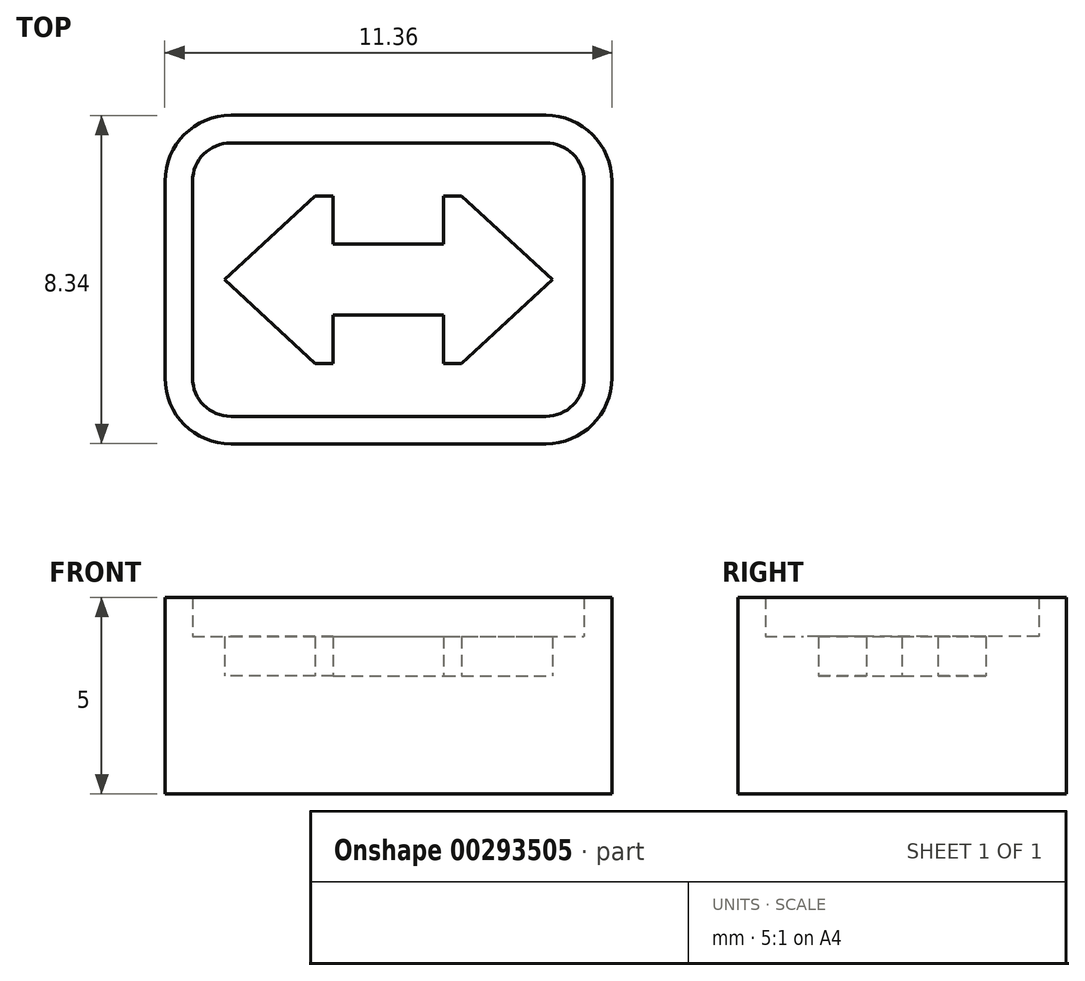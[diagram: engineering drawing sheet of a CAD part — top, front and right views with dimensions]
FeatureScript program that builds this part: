
annotation { "Feature Type Name" : "Feature", "Feature Type Description" : "" }
export const myFeature = defineFeature(function(context is Context, id is Id, definition is map)
    precondition{}
    {
        {
            var Q0;
            Q0=qCreatedBy(makeId("Top.planeOp"),FACE);
            var sketch = newSketch(context, id + "F0", { "sketchPlane" : qUnion([Q0])});
            skLineSegment(sketch, "E0", {"start": v(-1.4, -2.13) * mm, "end": v(-1.86, -2.13) * mm});
            skLineSegment(sketch, "E1", {"start": v(-1.86, -2.13) * mm, "end": v(-4.16, 0) * mm});
            skLineSegment(sketch, "E2", {"start": v(-4.16, 0) * mm, "end": v(-1.86, 2.13) * mm});
            skLineSegment(sketch, "E3", {"start": v(-1.86, 2.13) * mm, "end": v(-1.4, 2.13) * mm});
            skLineSegment(sketch, "E4", {"start": v(-1.4, 2.13) * mm, "end": v(-1.4, 0.9) * mm});
            skLineSegment(sketch, "E5", {"start": v(-1.4, 0.9) * mm, "end": v(1.4, 0.9) * mm});
            skLineSegment(sketch, "E6", {"start": v(1.4, 0.9) * mm, "end": v(1.4, 2.13) * mm});
            skLineSegment(sketch, "E7", {"start": v(1.4, 2.13) * mm, "end": v(1.86, 2.13) * mm});
            skLineSegment(sketch, "E8", {"start": v(1.86, 2.13) * mm, "end": v(4.16, 0) * mm});
            skLineSegment(sketch, "E9", {"start": v(4.16, 0) * mm, "end": v(1.86, -2.13) * mm});
            skLineSegment(sketch, "E10", {"start": v(1.86, -2.13) * mm, "end": v(1.4, -2.13) * mm});
            skLineSegment(sketch, "E11", {"start": v(1.4, -2.13) * mm, "end": v(1.4, -0.9) * mm});
            skLineSegment(sketch, "E12", {"start": v(1.4, -0.9) * mm, "end": v(-1.4, -0.9) * mm});
            skLineSegment(sketch, "E13", {"start": v(-1.4, -0.9) * mm, "end": v(-1.4, -2.13) * mm});
            skArc(sketch, "E14", {"start": v(4, -3.47) * mm, "mid": v(4.69, -3.19) * mm, "end": v(4.98, -2.5) * mm});
            skLineSegment(sketch, "E15", {"start": v(4.98, -2.5) * mm, "end": v(4.98, 2.5) * mm});
            skArc(sketch, "E16", {"start": v(4.98, 2.5) * mm, "mid": v(4.69, 3.19) * mm, "end": v(4, 3.47) * mm});
            skLineSegment(sketch, "E17", {"start": v(4, 3.48) * mm, "end": v(-4, 3.48) * mm});
            skArc(sketch, "E18", {"start": v(-4, 3.47) * mm, "mid": v(-4.69, 3.19) * mm, "end": v(-4.98, 2.5) * mm});
            skLineSegment(sketch, "E19", {"start": v(-4.97, 2.5) * mm, "end": v(-4.97, -2.5) * mm});
            skArc(sketch, "E20", {"start": v(-4.98, -2.5) * mm, "mid": v(-4.69, -3.19) * mm, "end": v(-4, -3.47) * mm});
            skLineSegment(sketch, "E21", {"start": v(-4, -3.47) * mm, "end": v(4, -3.47) * mm});
            skArc(sketch, "E22", {"start": v(4, -4.17) * mm, "mid": v(5.18, -3.68) * mm, "end": v(5.68, -2.5) * mm});
            skLineSegment(sketch, "E23", {"start": v(5.68, -2.5) * mm, "end": v(5.68, 2.5) * mm});
            skArc(sketch, "E24", {"start": v(5.68, 2.5) * mm, "mid": v(5.18, 3.68) * mm, "end": v(4, 4.17) * mm});
            skLineSegment(sketch, "E25", {"start": v(4, 4.18) * mm, "end": v(-4, 4.18) * mm});
            skArc(sketch, "E26", {"start": v(-4, 4.17) * mm, "mid": v(-5.18, 3.68) * mm, "end": v(-5.68, 2.5) * mm});
            skLineSegment(sketch, "E27", {"start": v(-5.68, 2.5) * mm, "end": v(-5.68, -2.5) * mm});
            skArc(sketch, "E28", {"start": v(-5.68, -2.5) * mm, "mid": v(-5.18, -3.68) * mm, "end": v(-4, -4.17) * mm});
            skLineSegment(sketch, "E29", {"start": v(-4, -4.18) * mm, "end": v(4, -4.18) * mm});
            skSolve(sketch);
        }
        {
            var Q0;
            Q0=makeQuery(id+"F0.imprint","IMPRINT",FACE,{"disambiguationData":[TD([[makeQuery(id+"F0.imprint","IMPRINT",EDGE,{"derivedFrom":sQuery(id+"F0.wireOp",EDGE,"E14")}),-1.0]])]});
            extrude(context, id + "F1", {"entities" : qUnion([Q0]), "depth" : 5 * mm});
        }
        {
            var Q0;
            Q0=makeQuery(id+"F0.imprint","IMPRINT",FACE,{"disambiguationData":[TD([[makeQuery(id+"F0.imprint","IMPRINT",EDGE,{"derivedFrom":sQuery(id+"F0.wireOp",EDGE,"E0")}),1.0]])]});
            extrude(context, id + "F2", {"entities" : qUnion([Q0]), "operationType" : NewBodyOperationType.ADD, "depth" : 4 * mm});
        }
        {
            var Q0;
            Q0=makeQuery(id+"F0.imprint","IMPRINT",FACE,{"disambiguationData":[TD([[makeQuery(id+"F0.imprint","IMPRINT",EDGE,{"derivedFrom":sQuery(id+"F0.wireOp",EDGE,"E0")}),-1.0]])]});
            extrude(context, id + "F3", {"entities" : qUnion([Q0]), "operationType" : NewBodyOperationType.ADD, "depth" : 3 * mm});
        }
    });
